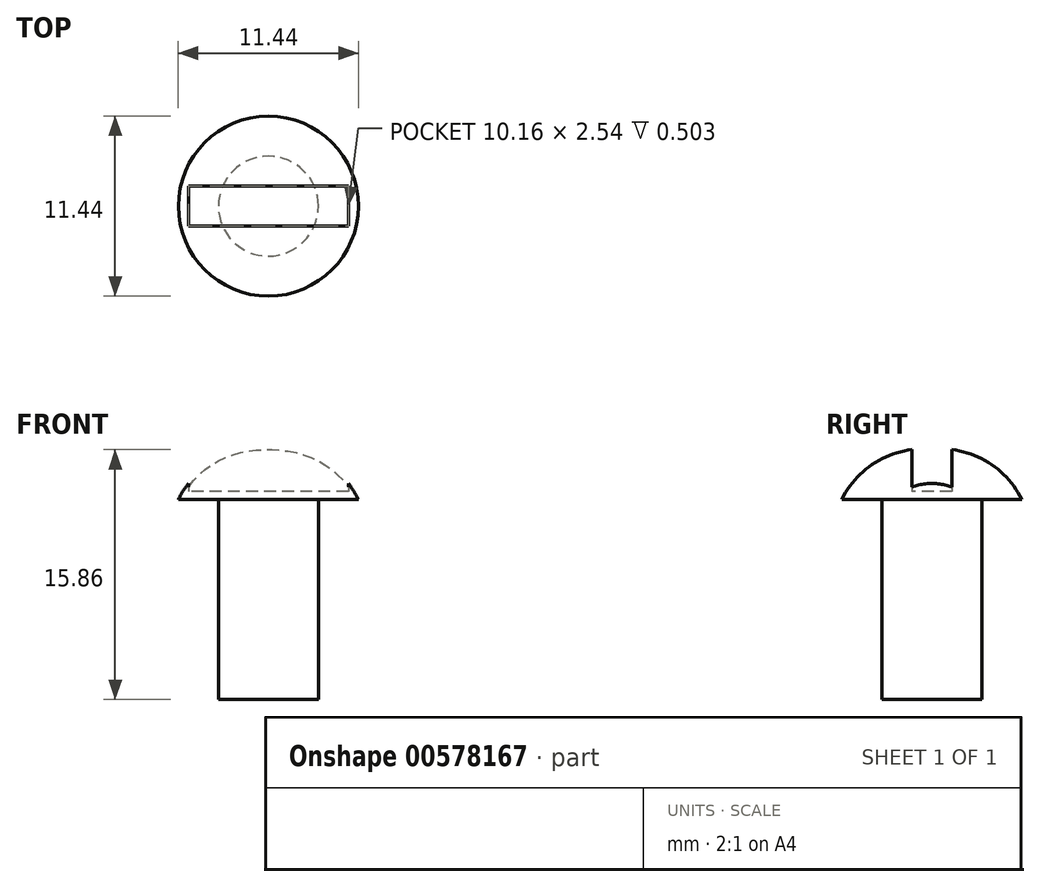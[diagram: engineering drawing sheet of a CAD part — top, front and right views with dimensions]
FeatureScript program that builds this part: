
annotation { "Feature Type Name" : "Feature", "Feature Type Description" : "" }
export const myFeature = defineFeature(function(context is Context, id is Id, definition is map)
    precondition{}
    {
        {
            var Q0;
            Q0=qCreatedBy(makeId("Front.planeOp"),FACE);
            var sketch = newSketch(context, id + "F0", { "sketchPlane" : qUnion([Q0])});
            skLineSegment(sketch, "E0", {"start": v(0, 0) * mm, "end": v(3.18, 0) * mm});
            skLineSegment(sketch, "E1", {"start": v(3.18, 0) * mm, "end": v(3.18, 12.7) * mm});
            skLineSegment(sketch, "E2", {"start": v(0, 0) * mm, "end": v(0, 15.88) * mm});
            skLineSegment(sketch, "E3", {"start": v(3.18, 12.7) * mm, "end": v(5.72, 12.7) * mm});
            skArc(sketch, "E4", {"start": v(5.72, 12.7) * mm, "mid": v(3.36, 15.19) * mm, "end": v(0, 15.88) * mm});
            skSolve(sketch);
        }
        {
            var Q0;
            Q0=makeQuery(id+"F0.imprint","IMPRINT",FACE,{"disambiguationData":[TD([[makeQuery(id+"F0.imprint","IMPRINT",EDGE,{"derivedFrom":sQuery(id+"F0.wireOp",EDGE,"E0")}),1.0]])]});
            var Q1;
            Q1=sQuery(id+"F0.wireOp",EDGE,"E2");
            revolve(context, id + "F1", {"entities" : qUnion([Q0]), "axis" : qUnion([Q1]), "revolveType" : RevolveType.FULL});
        }
        {
            var Q0;
            Q0=qCreatedBy(makeId("Top.planeOp"),FACE);
            cPlane(context, id + "F2", {"entities" : qUnion([Q0]), "cplaneType" : CPlaneType.OFFSET, "offset" : 13.2 * mm, "width" : 152.4 * mm, "height" : 152.4 * mm});
        }
        {
            var Q0;
            Q0=qCreatedBy(id+"F2.planeOp",FACE);
            var sketch = newSketch(context, id + "F3", { "sketchPlane" : qUnion([Q0])});
            skLineSegment(sketch, "E5", {"start": v(0, 0) * mm, "end": v(5.08, 0) * mm, "construction": true});
            skLineSegment(sketch, "E6", {"start": v(5.08, 0) * mm, "end": v(5.08, 1.27) * mm, "construction": true});
            skLineSegment(sketch, "E7.bottom", {"start": v(5.08, 1.27) * mm, "end": v(-5.08, 1.27) * mm});
            skLineSegment(sketch, "E7.top", {"start": v(5.08, -1.27) * mm, "end": v(-5.08, -1.27) * mm});
            skLineSegment(sketch, "E7.left", {"start": v(5.08, 1.27) * mm, "end": v(5.08, -1.27) * mm});
            skLineSegment(sketch, "E7.right", {"start": v(-5.08, 1.27) * mm, "end": v(-5.08, -1.27) * mm});
            skSolve(sketch);
        }
        {
            var Q0;
            Q0 = qSketchRegion(id + "F3", true);
            extrude(context, id + "F4", {"entities" : qUnion([Q0]), "operationType" : NewBodyOperationType.REMOVE, "endBound" : BoundingType.THROUGH_ALL, "depth" : 2.67 * mm, "offsetDistance" : 25.4 * mm});
        }
    });
